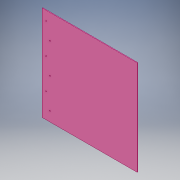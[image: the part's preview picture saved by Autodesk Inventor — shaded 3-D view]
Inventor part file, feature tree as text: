
AUTODESK INVENTOR PART (.ipt)
format: ipt  version: 2018 (Build 220112000, 112)  size: 108,544 bytes
history: native  units: mm
features: sketch x2, extrude x1, hole x1
ambient origin geometry x8: Origin, YZ Plane, XZ Plane, XY Plane, X Axis, Y Axis, Z Axis, Center Point
bodies: Solid1 (feature_tree)
feature tree (4):
  extrude  "Extrusion1"  Depth=250.0mm
  hole  "Hole1"  [1 undecoded]
  sketch  "Sketch1"  dims[d0=250.0mm d1=250.0mm]
  sketch  "Sketch2"  dims[d2=1.6mm d3=0.0mm d4=10.0mm d5=10.0mm d6=40.0mm d7=40.0mm d8=40.0mm d9=40.0mm d10=40.0mm d11=25.0mm d12=3.0mm d13=6.0mm d14=4.0mm d15=2.0mm d16=90.0deg d17=8.0mm d18=20.594885mm]
note: 1 required parameter value undecoded (feature->parameter linkage not recoverable at this tier; creation-order binding heuristic only, values carry confidence <= 0.55)
